# Revit family: IS_TonicII_R4338_BIM_FR
name_source: partatom
category: Plumbing Fixtures
revit_build: Autodesk Revit 2017 (Build: 20160225_1515(x64)
units: mm (PartAtom-declared; Revit-internal decimal feet)

## family parameters
Always vertical = No
Cut with Voids When Loaded = No
OmniClass Number = 23.40.20.00
OmniClass Title = General Furniture and Specialties
Part Type = Normal
Room Calculation Point = No
Round Connector Dimension = Use Diameter
Shared = No
Work Plane-Based = No

## types (5) — shared parameters
Accessoires = www.idealstandard.be
Auteur = Ideal Standard
BOSUseNativeGeometries = 1
Bim-NomDuProjet = ISI_IdealStandard_BathroomIntegratedFurniture_TonicII_R4338
Caractéristiques = TONIC II Plan étagère 45 cm
CodeBarre = 3391500572959
ConseilsDInstallation = www.idealstandard.be
DateDeCréation = 2018_08_15
Description = TONIC II Plan étagère 45 cm
Dimensions = 12 x 452 x 262 mm
Espace = Interne
Forme = rectangulaire
Hauteur = 12 mm  [stored 0.0393701 ft]
IfcExportAs = Bathroom integrated furniture
IfcExportType = IfcFurnitureType
InformationsProduit = www.idealstandard.be
Largeur = 452 mm  [stored 1.48294 ft]
LienUtile = www.idealstandard.be
Longueur = 262 mm  [stored 0.85958 ft]
Manufacturer = www.idealstandard.be
Marque = Ideal Standard
Matériel = 0
Nom = BathroomIntegratedFurniture_TonicII_R4338_IdealStandard
PoidsNet = 2,00 KG
Raccordement = Plomberie
Révision = 1
URL = www.idealstandard.be
Uniclass2015Code = Pr_40_30_78_05
Uniclass2015Title = Bathroom integrated furniture
Uniclass2015Version = Products v1.1
UnitéDeMesure = Millimètres
UnitéDeTemps = An
UnitéMonétaire = €
UrlDuFabricant = www.idealstandard.be
Version = 1
zero-valued in all types: Cost, CoûtDeRemplacement, Profondeur

## per-type parameters (varying)
| type | Couleur | Finition | Model |
| R4338FA - TONIC II PLAN ETAGERE L-MAINS GRIS BRILL | Gris | Gris | R4338FA |
| R4338FC - TONIC II PLAN ETAGERE L-MAINS SABLON BRI | Sablon Bris | Sablon Bris | R4338FC |
| R4338FE - TONIC II PLAN ETAGERE L-MAINS CHENE GRIS | Gris | Gris | R4338FE |
| R4338FF - TONIC II PLAN ETAGERE L-MAINS CHENE CERU | Ceru | Ceru | R4338FF |
| R4338WG - TONIC II PLAN ETAGERE L-MAINS BLANC BRIL | Blanc | Blanc | R4338WG |

note: [stored X ft] marks values corroborated as IEEE doubles in the binary element streams (Revit-internal decimal feet)

## geometry (parser evidence)
native form markers: Sweep x3
no freeform markers — native parametric forms only
